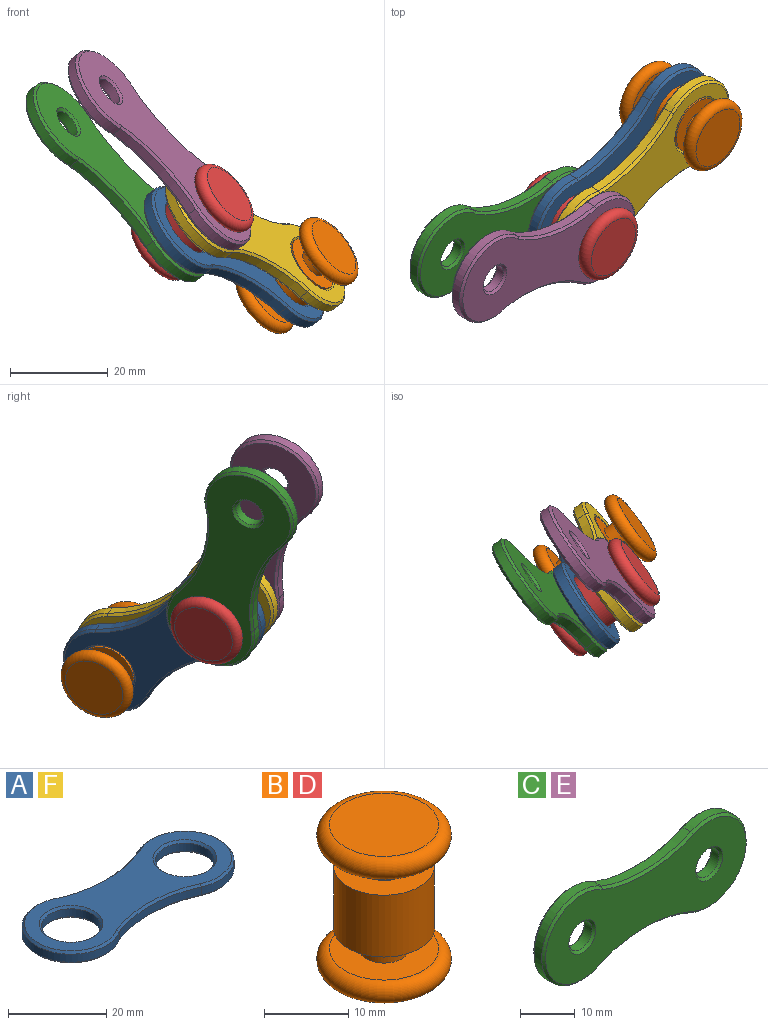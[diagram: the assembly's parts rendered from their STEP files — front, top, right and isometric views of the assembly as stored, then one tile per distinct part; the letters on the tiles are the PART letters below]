
ASSEMBLY  parts=6 mates=6
PART A: 20 faces, bbox 52.8x20x3 mm
  f0: cylinder r=30mm len=23.06mm, axis (0,0,-1), area 47.3mm2, adj f1,f5,f10,f15
  f1: cylinder r=10mm len=20mm, axis (0,0,-1), area 85.7mm2, adj f0,f2,f8,f13
  f2: cylinder r=30mm len=23.06mm, axis (0,0,-1), area 47.3mm2, adj f1,f5,f9,f12
  f3: cylinder r=6mm len=12mm, axis (0,0,-1), area 75.4mm2, adj f16,f17
  f4: cylinder r=6mm len=12mm, axis (0,0,-1), area 75.4mm2, adj f18,f19
  f5: cylinder r=10mm len=20mm, axis (0,0,-1), area 80.7mm2, adj f0,f2,f11,f14
  f6: plane 51.77x19mm, normal (0,0,1), area 500.8mm2, adj f12,f13,f14,f15,f17,f19
  f7: plane 51.77x19mm, normal (0,0,-1), area 500.8mm2, adj f8,f9,f10,f11,f16,f18
  f8: cone r=10mm half-angle=45deg, axis (0,0,1), area 29.6mm2, adj f1,f7,f9,f10
  f9: cone r=30.5mm half-angle=45deg, axis (0,0,-1), area 16.9mm2, adj f2,f7,f8,f11
  f10: cone r=30.5mm half-angle=45deg, axis (0,0,-1), area 16.9mm2, adj f0,f7,f8,f11
  f11: cone r=10mm half-angle=45deg, axis (0,0,1), area 27.8mm2, adj f5,f7,f9,f10
  f12: cone r=30mm half-angle=45deg, axis (0,0,1), area 16.9mm2, adj f2,f6,f13,f14
  f13: cone r=9.5mm half-angle=45deg, axis (0,0,-1), area 29.6mm2, adj f1,f6,f12,f15
  f14: cone r=9.5mm half-angle=45deg, axis (0,0,-1), area 27.8mm2, adj f5,f6,f12,f15
  f15: cone r=30mm half-angle=45deg, axis (0,0,1), area 16.9mm2, adj f0,f6,f13,f14
  f16: cone r=6.5mm half-angle=45deg, axis (0,0,-1), area 27.8mm2, adj f3,f7
  f17: cone r=6mm half-angle=45deg, axis (0,0,1), area 27.8mm2, adj f3,f6
  f18: cone r=6.5mm half-angle=45deg, axis (0,0,-1), area 27.8mm2, adj f4,f7
  f19: cone r=6mm half-angle=45deg, axis (0,0,1), area 27.8mm2, adj f4,f6
PART B: 11 faces, bbox 17.3x17.3x21 mm
  f0: plane 13x13mm, normal (0,0,1), area 104.5mm2, adj f2,f4
  f1: plane 13x13mm, normal (0,0,-1), area 132.7mm2, adj f2
  f2: torus R=6.5mm, axis (0,0,1), area 220.7mm2, adj f0,f1
  f3: plane 12x12mm, normal (0,0,-1), area 84.8mm2, adj f4,f5
  f4: cylinder r=3mm len=6mm, axis (0,0,1), area 56.5mm2, adj f0,f3
  f5: cylinder r=6mm len=12mm, axis (0,0,-1), area 339.3mm2, adj f3,f7
  f6: cylinder r=3mm len=6mm, axis (0,0,1), area 56.5mm2, adj f7,f10
  f7: plane 12x12mm, normal (0,0,1), area 84.8mm2, adj f5,f6
  f8: plane 13x13mm, normal (0,0,1), area 132.7mm2, adj f9
  f9: torus R=6.5mm, axis (0,0,1), area 220.7mm2, adj f8,f10
  f10: plane 13x13mm, normal (0,0,-1), area 104.5mm2, adj f6,f9
PART C: 20 faces, bbox 52.8x3x20 mm
  f0: cylinder r=30mm len=23.06mm, axis (0,1,0), area 47.3mm2, adj f1,f5,f13,f19
  f1: cylinder r=10mm len=20mm, axis (0,1,0), area 85.7mm2, adj f0,f2,f11,f17
  f2: cylinder r=30mm len=23.06mm, axis (0,1,0), area 47.3mm2, adj f1,f5,f10,f16
  f3: cylinder r=3mm len=6mm, axis (0,1,0), area 37.7mm2, adj f9,f15
  f4: cylinder r=3mm len=6mm, axis (0,1,0), area 37.7mm2, adj f8,f14
  f5: cylinder r=10mm len=20mm, axis (0,1,0), area 80.7mm2, adj f0,f2,f12,f18
  f6: plane 51.77x19mm, normal (0,-1,0), area 689.3mm2, adj f14,f15,f16,f17,f18,f19
  f7: plane 51.77x19mm, normal (0,1,0), area 689.3mm2, adj f8,f9,f10,f11,f12,f13
  f8: cone r=3.5mm half-angle=45deg, axis (0,1,0), area 14.4mm2, adj f4,f7
  f9: cone r=3.5mm half-angle=45deg, axis (0,1,0), area 14.4mm2, adj f3,f7
  f10: cone r=30.5mm half-angle=45deg, axis (0,1,0), area 16.9mm2, adj f2,f7,f11,f12
  f11: cone r=10mm half-angle=45deg, axis (0,-1,0), area 29.6mm2, adj f1,f7,f10,f13
  f12: cone r=10mm half-angle=45deg, axis (0,-1,0), area 27.8mm2, adj f5,f7,f10,f13
  f13: cone r=30.5mm half-angle=45deg, axis (0,1,0), area 16.9mm2, adj f0,f7,f11,f12
  f14: cone r=3mm half-angle=45deg, axis (0,-1,0), area 14.4mm2, adj f4,f6
  f15: cone r=3mm half-angle=45deg, axis (0,-1,0), area 14.4mm2, adj f3,f6
  f16: cone r=30mm half-angle=45deg, axis (0,-1,0), area 16.9mm2, adj f2,f6,f17,f18
  f17: cone r=9.5mm half-angle=45deg, axis (0,1,0), area 29.6mm2, adj f1,f6,f16,f19
  f18: cone r=9.5mm half-angle=45deg, axis (0,1,0), area 27.8mm2, adj f5,f6,f16,f19
  f19: cone r=30mm half-angle=45deg, axis (0,-1,0), area 16.9mm2, adj f0,f6,f17,f18
PART D: same geometry as B
PART E: same geometry as C
PART F: same geometry as A
PLACE A rot(axis=(0.65,0.57,0.5),66.6deg) t=(-44.32,-7.98,56.98)mm
PLACE B rot(axis=(0.07,0.78,-0.62),74.8deg) t=(-27.29,16.9,42.82)mm
PLACE C rot(axis=(-0.74,0.45,0.5),73.9deg) t=(-57.3,-10.58,66.62)mm
PLACE D rot(axis=(0.58,0.12,0.81),108.1deg) t=(-48.65,-5.44,53.7)mm
PLACE E rot(axis=(0.89,0.34,-0.3),127.3deg) t=(-46.48,-16.97,74.81)mm
PLACE F rot(axis=(0.65,0.57,0.5),66.6deg) t=(-39.99,-10.52,60.26)mm
MATE revolute E.f4 <-> D.f2  axis (0.72,-0.42,0.55) through (-36.74,-12.43,62.72)mm
MATE revolute A.f4 <-> B.f2  axis (-0.72,0.42,-0.55) through (-22.96,14.36,46.1)mm
MATE revolute D.f2 <-> C.f4  axis (0.72,-0.42,0.55) through (-45.4,-7.34,56.16)mm
MATE revolute A.f3 <-> D.f2  axis (-0.72,0.42,-0.55) through (-44.32,-7.98,56.98)mm
MATE revolute F.f4 <-> B.f2  axis (0.72,-0.42,0.55) through (-16.46,10.54,51.02)mm
MATE revolute F.f3 <-> D.f2  axis (0.72,-0.42,0.55) through (-37.82,-11.8,61.9)mm
